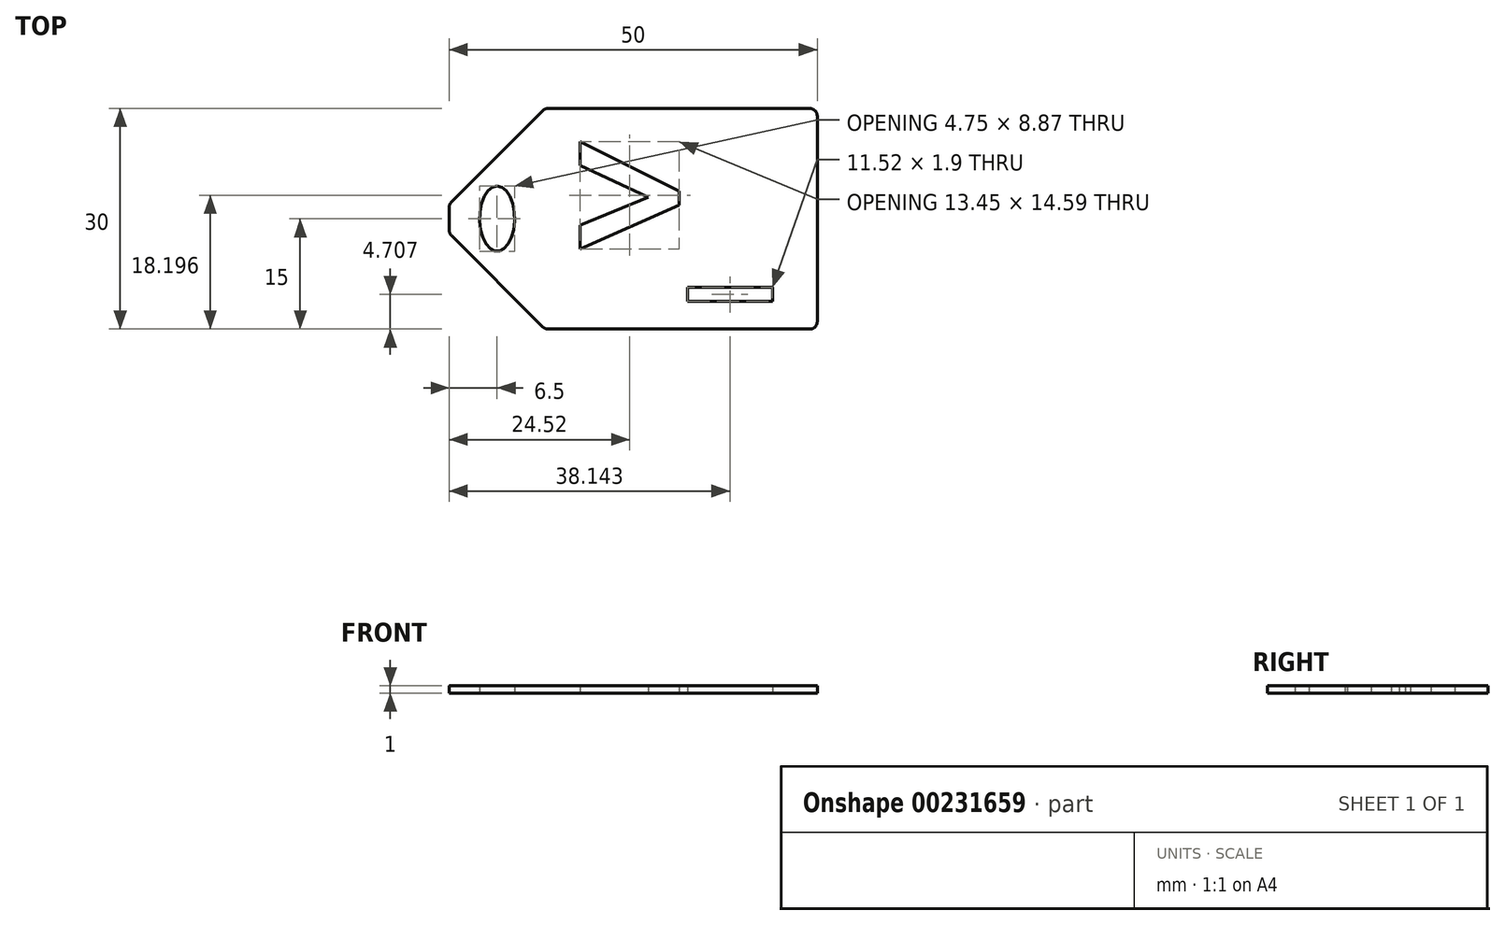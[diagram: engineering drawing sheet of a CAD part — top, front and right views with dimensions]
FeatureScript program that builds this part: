
annotation { "Feature Type Name" : "Feature", "Feature Type Description" : "" }
export const myFeature = defineFeature(function(context is Context, id is Id, definition is map)
    precondition{}
    {
        {
            var Q0;
            Q0=qCreatedBy(makeId("Top.planeOp"),FACE);
            var sketch = newSketch(context, id + "F0", { "sketchPlane" : qUnion([Q0])});
            skLineSegment(sketch, "E0.left", {"start": v(25, -14) * mm, "end": v(25, 14) * mm});
            skPoint(sketch, "E0.middle", {"position": v(0, 0) * mm});
            skPoint(sketch, "E1.visualSharp", {"position": v(25, 15) * mm});
            skArc(sketch, "E1.filletArc", {"start": v(25, 14) * mm, "mid": v(24.7, 14.7) * mm, "end": v(24, 15) * mm});
            skPoint(sketch, "E2.visualSharp", {"position": v(25, -15) * mm});
            skArc(sketch, "E2.filletArc", {"start": v(24, -15) * mm, "mid": v(24.7, -14.7) * mm, "end": v(25, -14) * mm});
            skText(sketch, "E3", { "text": ">_", "fontName": "OpenSans-Bold.ttf"});
            skPoint(sketch, "E4", {"position": v(-12, -15) * mm});
            skPoint(sketch, "E5", {"position": v(-12, 15) * mm});
            skPoint(sketch, "E6", {"position": v(-25, 2) * mm});
            skPoint(sketch, "E7", {"position": v(-25, -2) * mm});
            skLineSegment(sketch, "E8", {"start": v(-24.7, 2.29) * mm, "end": v(-12.3, 14.7) * mm});
            skLineSegment(sketch, "E9", {"start": v(-24.7, -2.29) * mm, "end": v(-12.3, -14.7) * mm});
            skLineSegment(sketch, "E10", {"start": v(-11.59, -15) * mm, "end": v(24, -15) * mm});
            skLineSegment(sketch, "E11", {"start": v(-11.59, 15) * mm, "end": v(24, 15) * mm});
            skLineSegment(sketch, "E12", {"start": v(-25, 1.58) * mm, "end": v(-25, -1.58) * mm});
            skArc(sketch, "E13.filletArc", {"start": v(-12.3, -14.7) * mm, "mid": v(-11.97, -14.92) * mm, "end": v(-11.59, -15) * mm});
            skArc(sketch, "E14.filletArc", {"start": v(-11.59, 15) * mm, "mid": v(-11.97, 14.92) * mm, "end": v(-12.3, 14.7) * mm});
            skArc(sketch, "E15.filletArc", {"start": v(-25, -1.58) * mm, "mid": v(-24.92, -1.96) * mm, "end": v(-24.7, -2.29) * mm});
            skArc(sketch, "E16.filletArc", {"start": v(-24.7, 2.29) * mm, "mid": v(-24.92, 1.96) * mm, "end": v(-25, 1.58) * mm});
            skLineSegment(sketch, "E17", {"start": v(-12, 15) * mm, "end": v(-12, -15) * mm});
            skPoint(sketch, "E18", {"position": v(-12, 0) * mm});
            skLineSegment(sketch, "E19", {"start": v(-25, 0) * mm, "end": v(-12, 0) * mm});
            skEllipse(sketch, "E20", {"center": v(-18.5, 0) * mm, "majorRadius": 4.44 * mm, "minorRadius": 2.38 * mm, "majorAxis": v(0, 1)});
            const initialGuessF0  = {"E3": [-0.0084, -0.00685, 1, 0, 0.01998]};
            skSetInitialGuess(sketch, initialGuessF0);
            skSolve(sketch);
        }
        {
            var Q0;
            Q0 = qSketchRegion(id + "F0", true);
            extrude(context, id + "F1", {"entities" : qUnion([Q0]), "depth" : 1 * mm});
        }
    });
